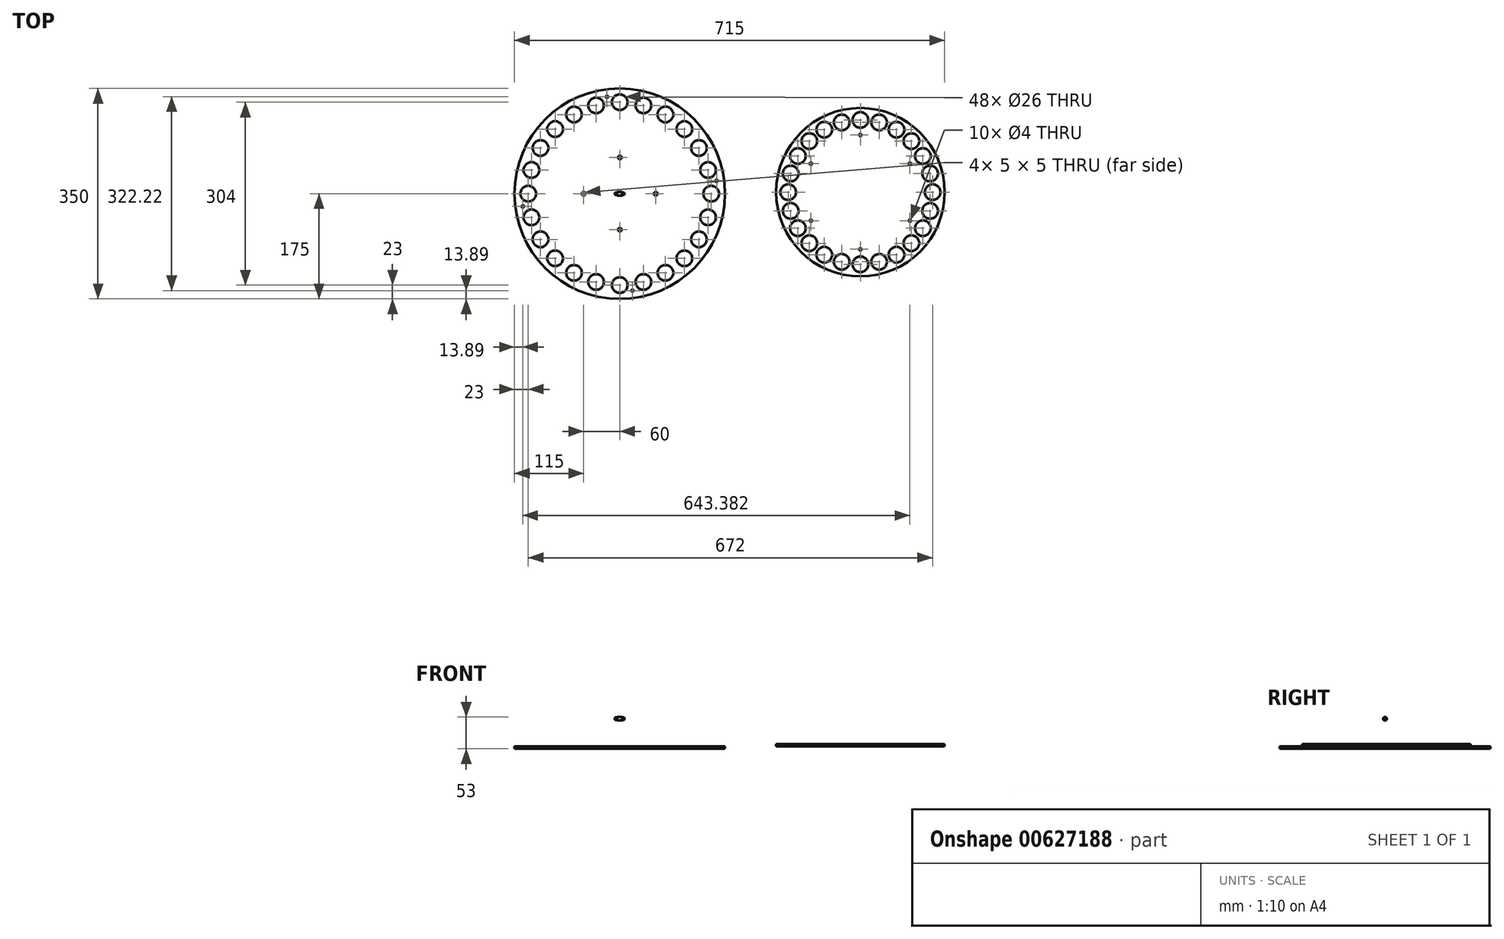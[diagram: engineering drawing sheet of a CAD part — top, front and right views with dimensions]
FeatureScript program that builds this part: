
annotation { "Feature Type Name" : "Feature", "Feature Type Description" : "" }
export const myFeature = defineFeature(function(context is Context, id is Id, definition is map)
    precondition{}
    {
        {
            var Q0;
            Q0=qCreatedBy(makeId("Top.planeOp"),FACE);
            var sketch = newSketch(context, id + "F0", { "sketchPlane" : qUnion([Q0])});
            skCircle(sketch, "E0", {"center": v(0, 0) * mm, "radius": 175 * mm});
            skLineSegment(sketch, "E1", {"start": v(0, 210.07) * mm, "end": v(0, -239.93) * mm, "construction": true});
            skLineSegment(sketch, "E2", {"start": v(-226.4, 0) * mm, "end": v(223.6, 0) * mm, "construction": true});
            skCircle(sketch, "E3", {"center": v(0, 152) * mm, "radius": 13 * mm});
            skCircle(sketch, "E4.1.1", {"center": v(-39.34, 146.82) * mm, "radius": 13 * mm});
            skCircle(sketch, "E4.2.1", {"center": v(-76, 131.64) * mm, "radius": 13 * mm});
            skCircle(sketch, "E4.3.1", {"center": v(-107.48, 107.48) * mm, "radius": 13 * mm});
            skCircle(sketch, "E4.4.1", {"center": v(-131.64, 76) * mm, "radius": 13 * mm});
            skCircle(sketch, "E4.5.1", {"center": v(-146.82, 39.34) * mm, "radius": 13 * mm});
            skCircle(sketch, "E4.6.1", {"center": v(-152, 0) * mm, "radius": 13 * mm});
            skCircle(sketch, "E4.7.1", {"center": v(-146.82, -39.34) * mm, "radius": 13 * mm});
            skCircle(sketch, "E4.8.1", {"center": v(-131.64, -76) * mm, "radius": 13 * mm});
            skCircle(sketch, "E4.9.1", {"center": v(-107.48, -107.48) * mm, "radius": 13 * mm});
            skCircle(sketch, "E4.10.1", {"center": v(-76, -131.64) * mm, "radius": 13 * mm});
            skCircle(sketch, "E4.11.1", {"center": v(-39.34, -146.82) * mm, "radius": 13 * mm});
            skCircle(sketch, "E4.12.1", {"center": v(0, -152) * mm, "radius": 13 * mm});
            skCircle(sketch, "E4.13.1", {"center": v(39.34, -146.82) * mm, "radius": 13 * mm});
            skCircle(sketch, "E4.14.1", {"center": v(76, -131.64) * mm, "radius": 13 * mm});
            skCircle(sketch, "E4.15.1", {"center": v(107.48, -107.48) * mm, "radius": 13 * mm});
            skCircle(sketch, "E4.16.1", {"center": v(131.64, -76) * mm, "radius": 13 * mm});
            skCircle(sketch, "E4.17.1", {"center": v(146.82, -39.34) * mm, "radius": 13 * mm});
            skCircle(sketch, "E4.18.1", {"center": v(152, 0) * mm, "radius": 13 * mm});
            skCircle(sketch, "E4.19.1", {"center": v(146.82, 39.34) * mm, "radius": 13 * mm});
            skCircle(sketch, "E4.20.1", {"center": v(131.64, 76) * mm, "radius": 13 * mm});
            skCircle(sketch, "E4.21.1", {"center": v(107.48, 107.48) * mm, "radius": 13 * mm});
            skCircle(sketch, "E4.22.1", {"center": v(76, 131.64) * mm, "radius": 13 * mm});
            skCircle(sketch, "E4.23.1", {"center": v(39.34, 146.82) * mm, "radius": 13 * mm});
            skLineSegment(sketch, "E5", {"start": v(0, 0) * mm, "end": v(223.08, 29.37) * mm, "construction": true});
            skCircle(sketch, "E6", {"center": v(161.1, 21.21) * mm, "radius": 2 * mm});
            skLineSegment(sketch, "E7", {"start": v(0, 0) * mm, "end": v(-29.37, 223.08) * mm, "construction": true});
            skLineSegment(sketch, "E8", {"start": v(0, 0) * mm, "end": v(-223.08, -29.37) * mm, "construction": true});
            skLineSegment(sketch, "E9", {"start": v(0, 0) * mm, "end": v(29.37, -223.08) * mm, "construction": true});
            skCircle(sketch, "E10", {"center": v(-21.21, 161.1) * mm, "radius": 2 * mm});
            skCircle(sketch, "E11", {"center": v(-161.1, -21.21) * mm, "radius": 2 * mm});
            skCircle(sketch, "E12", {"center": v(21.21, -161.1) * mm, "radius": 2 * mm});
            skLineSegment(sketch, "E13.bottom", {"start": v(2.5, 57.5) * mm, "end": v(-2.5, 57.5) * mm});
            skLineSegment(sketch, "E13.top", {"start": v(2.5, 62.5) * mm, "end": v(-2.5, 62.5) * mm});
            skLineSegment(sketch, "E13.left", {"start": v(2.5, 57.5) * mm, "end": v(2.5, 62.5) * mm});
            skLineSegment(sketch, "E13.right", {"start": v(-2.5, 57.5) * mm, "end": v(-2.5, 62.5) * mm});
            skPoint(sketch, "E13.middle", {"position": v(0, 60) * mm});
            skLineSegment(sketch, "E14.bottom", {"start": v(62.5, -2.5) * mm, "end": v(57.5, -2.5) * mm});
            skLineSegment(sketch, "E14.top", {"start": v(62.5, 2.5) * mm, "end": v(57.5, 2.5) * mm});
            skLineSegment(sketch, "E14.left", {"start": v(62.5, -2.5) * mm, "end": v(62.5, 2.5) * mm});
            skLineSegment(sketch, "E14.right", {"start": v(57.5, -2.5) * mm, "end": v(57.5, 2.5) * mm});
            skPoint(sketch, "E14.middle", {"position": v(60, 0) * mm});
            skLineSegment(sketch, "E15.bottom", {"start": v(-57.5, 2.5) * mm, "end": v(-62.5, 2.5) * mm});
            skLineSegment(sketch, "E15.top", {"start": v(-57.5, -2.5) * mm, "end": v(-62.5, -2.5) * mm});
            skLineSegment(sketch, "E15.left", {"start": v(-57.5, 2.5) * mm, "end": v(-57.5, -2.5) * mm});
            skLineSegment(sketch, "E15.right", {"start": v(-62.5, 2.5) * mm, "end": v(-62.5, -2.5) * mm});
            skPoint(sketch, "E15.middle", {"position": v(-60, 0) * mm});
            skLineSegment(sketch, "E16.bottom", {"start": v(-2.5, -57.5) * mm, "end": v(2.5, -57.5) * mm});
            skLineSegment(sketch, "E16.top", {"start": v(-2.5, -62.5) * mm, "end": v(2.5, -62.5) * mm});
            skLineSegment(sketch, "E16.left", {"start": v(-2.5, -57.5) * mm, "end": v(-2.5, -62.5) * mm});
            skLineSegment(sketch, "E16.right", {"start": v(2.5, -57.5) * mm, "end": v(2.5, -62.5) * mm});
            skPoint(sketch, "E16.middle", {"position": v(0, -60) * mm});
            skSolve(sketch);
        }
        {
            var Q0;
            Q0=makeQuery(id+"F0.imprint","IMPRINT",FACE,{"disambiguationData":[TD([[makeQuery(id+"F0.imprint","IMPRINT",EDGE,{"derivedFrom":sQuery(id+"F0.wireOp",EDGE,"E3")}),-1.0]])]});
            extrude(context, id + "F1", {"entities" : qUnion([Q0]), "depth" : 4 * mm, "offsetDistance" : 25 * mm});
        }
        {
            var Q0;
            Q0=qCreatedBy(makeId("Right.planeOp"),FACE);
            var sketch = newSketch(context, id + "F2", { "sketchPlane" : qUnion([Q0])});
            skLineSegment(sketch, "E17", {"start": v(0, 0) * mm, "end": v(0, 85) * mm, "construction": true});
            skCircle(sketch, "E18", {"center": v(0, 50) * mm, "radius": 3 * mm});
            skCircle(sketch, "E19", {"center": v(0, 50) * mm, "radius": 2 * mm});
            skSolve(sketch);
        }
        {
            var Q0;
            Q0=makeQuery(id+"F2.imprint","IMPRINT",FACE,{"disambiguationData":[TD([[makeQuery(id+"F2.imprint","IMPRINT",EDGE,{"derivedFrom":sQuery(id+"F2.wireOp",EDGE,"E18")}),1.0]])]});
            extrude(context, id + "F3", {"entities" : qUnion([Q0]), "depth" : 8 * mm, "offsetDistance" : 25 * mm, "symmetric" : true});
        }
        {
            var Q0;
            Q0=makeQuery(id+"F2.imprint","IMPRINT",FACE,{"disambiguationData":[TD([[makeQuery(id+"F2.imprint","IMPRINT",EDGE,{"derivedFrom":sQuery(id+"F2.wireOp",EDGE,"E19")}),1.0]])]});
            extrude(context, id + "F4", {"entities" : qUnion([Q0]), "operationType" : NewBodyOperationType.ADD, "depth" : 16 * mm, "offsetDistance" : 25 * mm, "symmetric" : true});
        }
        {
            var Q0;
            Q0=makeQuery(id+"F1.opExtrude","CAP_FACE",FACE,{"disambiguationData":[OSD([sQuery(id+"F0.wireOp",EDGE,"E3"),sQuery(id+"F0.wireOp",EDGE,"E4.1.1"),sQuery(id+"F0.wireOp",EDGE,"E4.2.1"),sQuery(id+"F0.wireOp",EDGE,"E4.3.1"),sQuery(id+"F0.wireOp",EDGE,"E4.4.1"),sQuery(id+"F0.wireOp",EDGE,"E4.5.1"),sQuery(id+"F0.wireOp",EDGE,"E4.6.1"),sQuery(id+"F0.wireOp",EDGE,"E4.7.1"),sQuery(id+"F0.wireOp",EDGE,"E4.8.1"),sQuery(id+"F0.wireOp",EDGE,"E4.9.1"),sQuery(id+"F0.wireOp",EDGE,"E4.10.1"),sQuery(id+"F0.wireOp",EDGE,"E4.11.1"),sQuery(id+"F0.wireOp",EDGE,"E4.12.1"),sQuery(id+"F0.wireOp",EDGE,"E4.13.1"),sQuery(id+"F0.wireOp",EDGE,"E4.14.1"),sQuery(id+"F0.wireOp",EDGE,"E4.15.1"),sQuery(id+"F0.wireOp",EDGE,"E4.16.1"),sQuery(id+"F0.wireOp",EDGE,"E4.17.1"),sQuery(id+"F0.wireOp",EDGE,"E4.18.1"),sQuery(id+"F0.wireOp",EDGE,"E4.19.1"),sQuery(id+"F0.wireOp",EDGE,"E4.20.1"),sQuery(id+"F0.wireOp",EDGE,"E4.21.1"),sQuery(id+"F0.wireOp",EDGE,"E4.22.1"),sQuery(id+"F0.wireOp",EDGE,"E0"),sQuery(id+"F0.wireOp",EDGE,"E4.23.1"),sQuery(id+"F0.wireOp",EDGE,"E6"),sQuery(id+"F0.wireOp",EDGE,"E10"),sQuery(id+"F0.wireOp",EDGE,"E11"),sQuery(id+"F0.wireOp",EDGE,"E12"),sQuery(id+"F0.wireOp",EDGE,"E13.bottom"),sQuery(id+"F0.wireOp",EDGE,"E13.top"),sQuery(id+"F0.wireOp",EDGE,"E13.left"),sQuery(id+"F0.wireOp",EDGE,"E13.right"),sQuery(id+"F0.wireOp",EDGE,"E14.bottom"),sQuery(id+"F0.wireOp",EDGE,"E14.top"),sQuery(id+"F0.wireOp",EDGE,"E14.left"),sQuery(id+"F0.wireOp",EDGE,"E14.right"),sQuery(id+"F0.wireOp",EDGE,"E15.bottom"),sQuery(id+"F0.wireOp",EDGE,"E15.top"),sQuery(id+"F0.wireOp",EDGE,"E15.left"),sQuery(id+"F0.wireOp",EDGE,"E15.right"),sQuery(id+"F0.wireOp",EDGE,"E16.bottom"),sQuery(id+"F0.wireOp",EDGE,"E16.top"),sQuery(id+"F0.wireOp",EDGE,"E16.left"),sQuery(id+"F0.wireOp",EDGE,"E16.right")])],"isStart":false});
            var sketch = newSketch(context, id + "F5", { "sketchPlane" : qUnion([Q0])});
            skCircle(sketch, "E20", {"center": v(400, 2.5) * mm, "radius": 140 * mm});
            skCircle(sketch, "E21", {"center": v(400, 122.5) * mm, "radius": 13 * mm});
            skCircle(sketch, "E22.1.0", {"center": v(368.94, 118.41) * mm, "radius": 13 * mm});
            skCircle(sketch, "E22.2.0", {"center": v(340, 106.42) * mm, "radius": 13 * mm});
            skCircle(sketch, "E22.3.0", {"center": v(315.15, 87.35) * mm, "radius": 13 * mm});
            skCircle(sketch, "E22.4.0", {"center": v(296.08, 62.5) * mm, "radius": 13 * mm});
            skCircle(sketch, "E22.5.0", {"center": v(284.09, 33.56) * mm, "radius": 13 * mm});
            skCircle(sketch, "E22.6.0", {"center": v(280, 2.5) * mm, "radius": 13 * mm});
            skCircle(sketch, "E22.7.0", {"center": v(284.09, -28.56) * mm, "radius": 13 * mm});
            skCircle(sketch, "E22.8.0", {"center": v(296.08, -57.5) * mm, "radius": 13 * mm});
            skCircle(sketch, "E22.9.0", {"center": v(315.15, -82.35) * mm, "radius": 13 * mm});
            skCircle(sketch, "E22.10.0", {"center": v(340, -101.42) * mm, "radius": 13 * mm});
            skCircle(sketch, "E22.11.0", {"center": v(368.94, -113.41) * mm, "radius": 13 * mm});
            skCircle(sketch, "E22.12.0", {"center": v(400, -117.5) * mm, "radius": 13 * mm});
            skCircle(sketch, "E22.13.0", {"center": v(431.06, -113.41) * mm, "radius": 13 * mm});
            skCircle(sketch, "E22.14.0", {"center": v(460, -101.42) * mm, "radius": 13 * mm});
            skCircle(sketch, "E22.15.0", {"center": v(484.85, -82.35) * mm, "radius": 13 * mm});
            skCircle(sketch, "E22.16.0", {"center": v(503.92, -57.5) * mm, "radius": 13 * mm});
            skCircle(sketch, "E22.17.0", {"center": v(515.91, -28.56) * mm, "radius": 13 * mm});
            skCircle(sketch, "E22.18.0", {"center": v(520, 2.5) * mm, "radius": 13 * mm});
            skCircle(sketch, "E22.19.0", {"center": v(515.91, 33.56) * mm, "radius": 13 * mm});
            skCircle(sketch, "E22.20.0", {"center": v(503.92, 62.5) * mm, "radius": 13 * mm});
            skCircle(sketch, "E22.21.0", {"center": v(484.85, 87.35) * mm, "radius": 13 * mm});
            skCircle(sketch, "E22.22.0", {"center": v(460, 106.42) * mm, "radius": 13 * mm});
            skCircle(sketch, "E22.23.0", {"center": v(431.06, 118.41) * mm, "radius": 13 * mm});
            skLineSegment(sketch, "E23", {"start": v(600, 136.3) * mm, "end": v(600, -133.7) * mm, "construction": true});
            skCircle(sketch, "E24", {"center": v(400, 97.5) * mm, "radius": 2 * mm});
            skCircle(sketch, "E25.1.0", {"center": v(317.73, 50) * mm, "radius": 2 * mm});
            skCircle(sketch, "E25.2.0", {"center": v(317.73, -45) * mm, "radius": 2 * mm});
            skCircle(sketch, "E25.3.0", {"center": v(400, -92.5) * mm, "radius": 2 * mm});
            skCircle(sketch, "E25.4.0", {"center": v(482.27, -45) * mm, "radius": 2 * mm});
            skCircle(sketch, "E25.5.0", {"center": v(482.27, 50) * mm, "radius": 2 * mm});
            skCircle(sketch, "E26.MirrorC", {"center": v(800, 2.5) * mm, "radius": 140 * mm});
            skCircle(sketch, "E27.MirrorC", {"center": v(717.73, 50) * mm, "radius": 2 * mm});
            skCircle(sketch, "E28.MirrorC", {"center": v(717.73, -45) * mm, "radius": 2 * mm});
            skCircle(sketch, "E29.MirrorC", {"center": v(800, 97.5) * mm, "radius": 2 * mm});
            skCircle(sketch, "E30.MirrorC", {"center": v(800, -92.5) * mm, "radius": 2 * mm});
            skCircle(sketch, "E31.MirrorC", {"center": v(882.27, -45) * mm, "radius": 2 * mm});
            skCircle(sketch, "E32.MirrorC", {"center": v(882.27, 50) * mm, "radius": 2 * mm});
            skCircle(sketch, "E33", {"center": v(800, 59.1) * mm, "radius": 2.05 * mm});
            skCircle(sketch, "E34.1.0", {"center": v(743.4, 2.5) * mm, "radius": 2.05 * mm});
            skCircle(sketch, "E34.2.0", {"center": v(800, -54.1) * mm, "radius": 2.05 * mm});
            skCircle(sketch, "E34.3.0", {"center": v(856.6, 2.5) * mm, "radius": 2.05 * mm});
            skSolve(sketch);
        }
        {
            var Q0;
            Q0=makeQuery(id+"F5.imprint","IMPRINT",FACE,{"disambiguationData":[TD([[makeQuery(id+"F5.imprint","IMPRINT",EDGE,{"derivedFrom":sQuery(id+"F5.wireOp",EDGE,"E20")}),1.0]])]});
            var Q1;
            Q1=makeQuery(id+"F5.imprint","IMPRINT",FACE,{"disambiguationData":[TD([[makeQuery(id+"F5.imprint","IMPRINT",EDGE,{"derivedFrom":sQuery(id+"F5.wireOp",EDGE,"E26.MirrorC")}),-1.0]])]});
            extrude(context, id + "F6", {"entities" : qUnion([Q0, Q1]), "depth" : 4 * mm, "offsetDistance" : 25 * mm});
        }
    });
